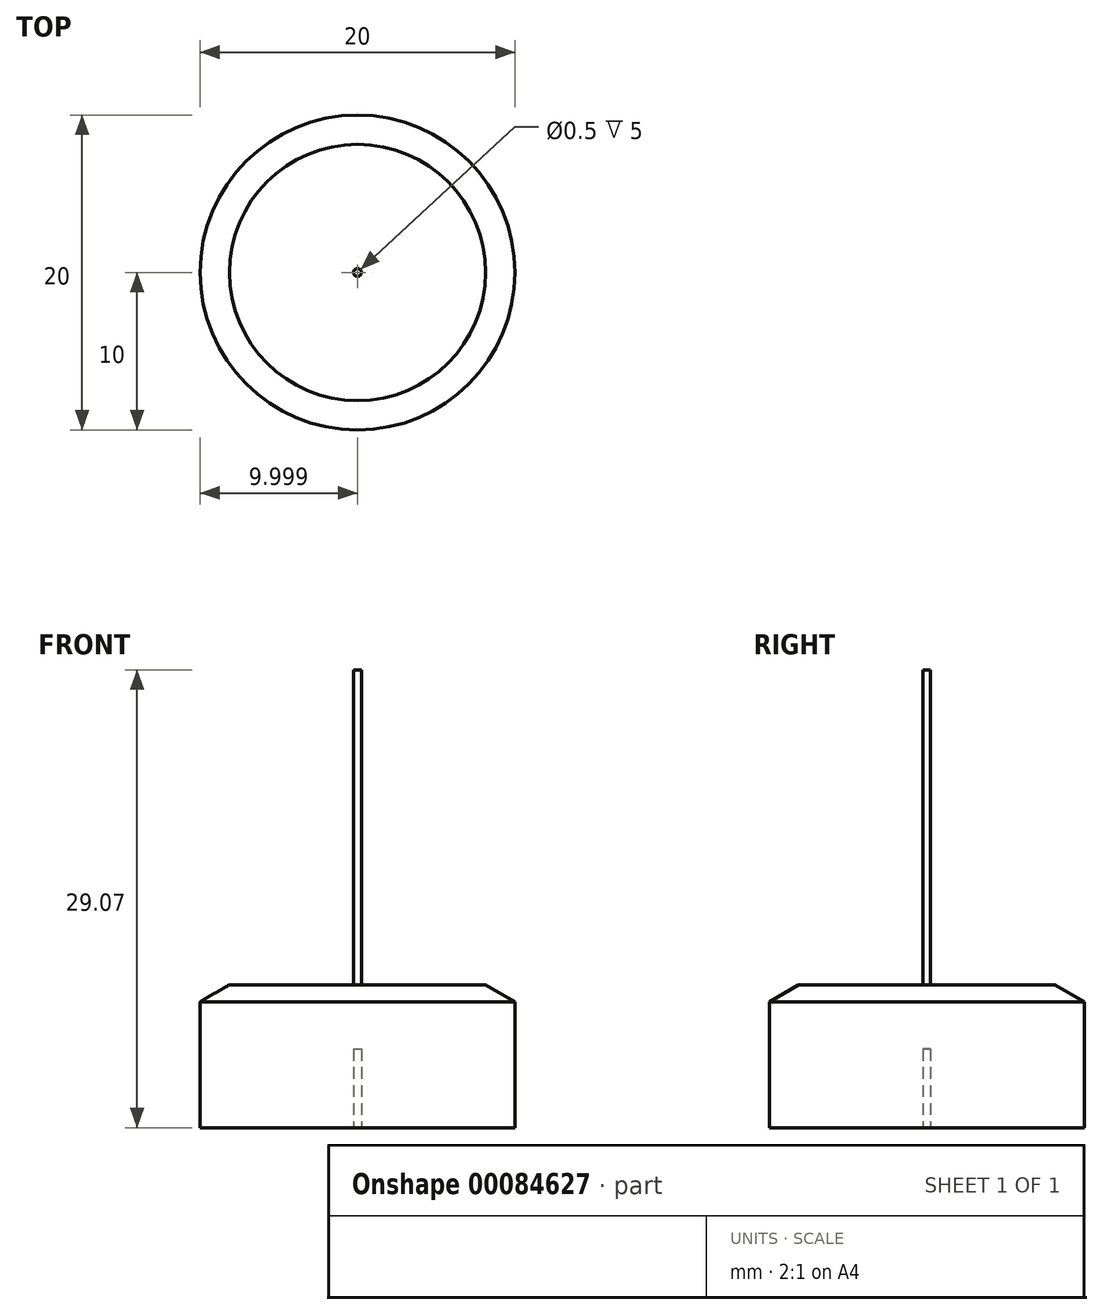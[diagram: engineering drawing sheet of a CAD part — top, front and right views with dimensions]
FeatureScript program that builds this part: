
annotation { "Feature Type Name" : "Feature", "Feature Type Description" : "" }
export const myFeature = defineFeature(function(context is Context, id is Id, definition is map)
    precondition{}
    {
        {
            var Q0;
            Q0=qCreatedBy(makeId("Front.planeOp"),FACE);
            var sketch = newSketch(context, id + "F0", { "sketchPlane" : qUnion([Q0])});
            skLineSegment(sketch, "E0.bottom", {"start": v(-30.55, 8) * mm, "end": v(-20.55, 8) * mm});
            skLineSegment(sketch, "E0.top", {"start": v(-30.55, 0) * mm, "end": v(-20.8, 0) * mm});
            skLineSegment(sketch, "E0.left", {"start": v(-30.55, 8) * mm, "end": v(-30.55, 0) * mm});
            skPoint(sketch, "E1", {"position": v(-20.55, 8) * mm});
            skPoint(sketch, "E2", {"position": v(-20.55, 0) * mm});
            skPoint(sketch, "E3", {"position": v(-20.55, 9.07) * mm});
            skLineSegment(sketch, "E4", {"start": v(-20.55, 8) * mm, "end": v(-20.55, 9.07) * mm});
            skLineSegment(sketch, "E5", {"start": v(-30.55, 8) * mm, "end": v(-28.7, 9.07) * mm});
            skLineSegment(sketch, "E6", {"start": v(-28.7, 9.07) * mm, "end": v(-20.55, 9.07) * mm});
            skLineSegment(sketch, "E7", {"start": v(-20.55, 8) * mm, "end": v(-20.55, 5) * mm});
            skPoint(sketch, "E0.right.end.orphan", {"position": v(-10.55, 0) * mm});
            skPoint(sketch, "E8.start.orphan", {"position": v(-10.55, 8) * mm});
            skLineSegment(sketch, "E9", {"start": v(-20.55, 9.07) * mm, "end": v(-20.55, 29.07) * mm});
            skLineSegment(sketch, "E10", {"start": v(-20.55, 29.07) * mm, "end": v(-20.8, 29.07) * mm});
            skLineSegment(sketch, "E11", {"start": v(-20.8, 29.07) * mm, "end": v(-20.8, 0) * mm});
            skPoint(sketch, "E12.start.orphan", {"position": v(-20.55, 4) * mm});
            skLineSegment(sketch, "E13", {"start": v(-20.55, 5) * mm, "end": v(-20.8, 5) * mm});
            skPoint(sketch, "E14", {"position": v(-20.55, 5) * mm});
            skSolve(sketch);
        }
        {
            var Q0;
            {var subQ0=sQuery(id+"F0.wireOp",EDGE,"E9");Q0=makeQuery(id+"F0.imprint","IMPRINT",FACE,{"disambiguationData":[TD([[makeQuery(id+"F0.imprint","IMPRINT",EDGE,{"derivedFrom":subQ0}),1.0]])]});}
            var Q1;
            {var subQ5=sQuery(id+"F0.wireOp",EDGE,"E0.top");Q1=makeQuery(id+"F0.imprint","IMPRINT",FACE,{"disambiguationData":[TD([[makeQuery(id+"F0.imprint","IMPRINT",EDGE,{"derivedFrom":subQ5}),1.0]])]});}
            var Q2;
            {var subQ0=sQuery(id+"F0.wireOp",EDGE,"E5");Q2=makeQuery(id+"F0.imprint","IMPRINT",FACE,{"disambiguationData":[TD([[makeQuery(id+"F0.imprint","IMPRINT",EDGE,{"derivedFrom":subQ0}),-1.0]])]});}
            var Q3;
            {var subQ0=sQuery(id+"F0.wireOp",EDGE,"E7");Q3=makeQuery(id+"F0.imprint","IMPRINT",FACE,{"disambiguationData":[TD([[makeQuery(id+"F0.imprint","IMPRINT",EDGE,{"derivedFrom":subQ0}),-1.0]])]});}
            var Q4;
            {var subQ0=sQuery(id+"F0.wireOp",EDGE,"E4");Q4=makeQuery(id+"F0.imprint","IMPRINT",FACE,{"disambiguationData":[TD([[makeQuery(id+"F0.imprint","IMPRINT",EDGE,{"derivedFrom":subQ0}),1.0]])]});}
            var Q5;
            Q5=sQuery(id+"F0.wireOp",EDGE,"E9");
            revolve(context, id + "F1", {"entities" : qUnion([Q0, Q1, Q2, Q3, Q4]), "axis" : qUnion([Q5]), "revolveType" : RevolveType.FULL});
        }
    });
